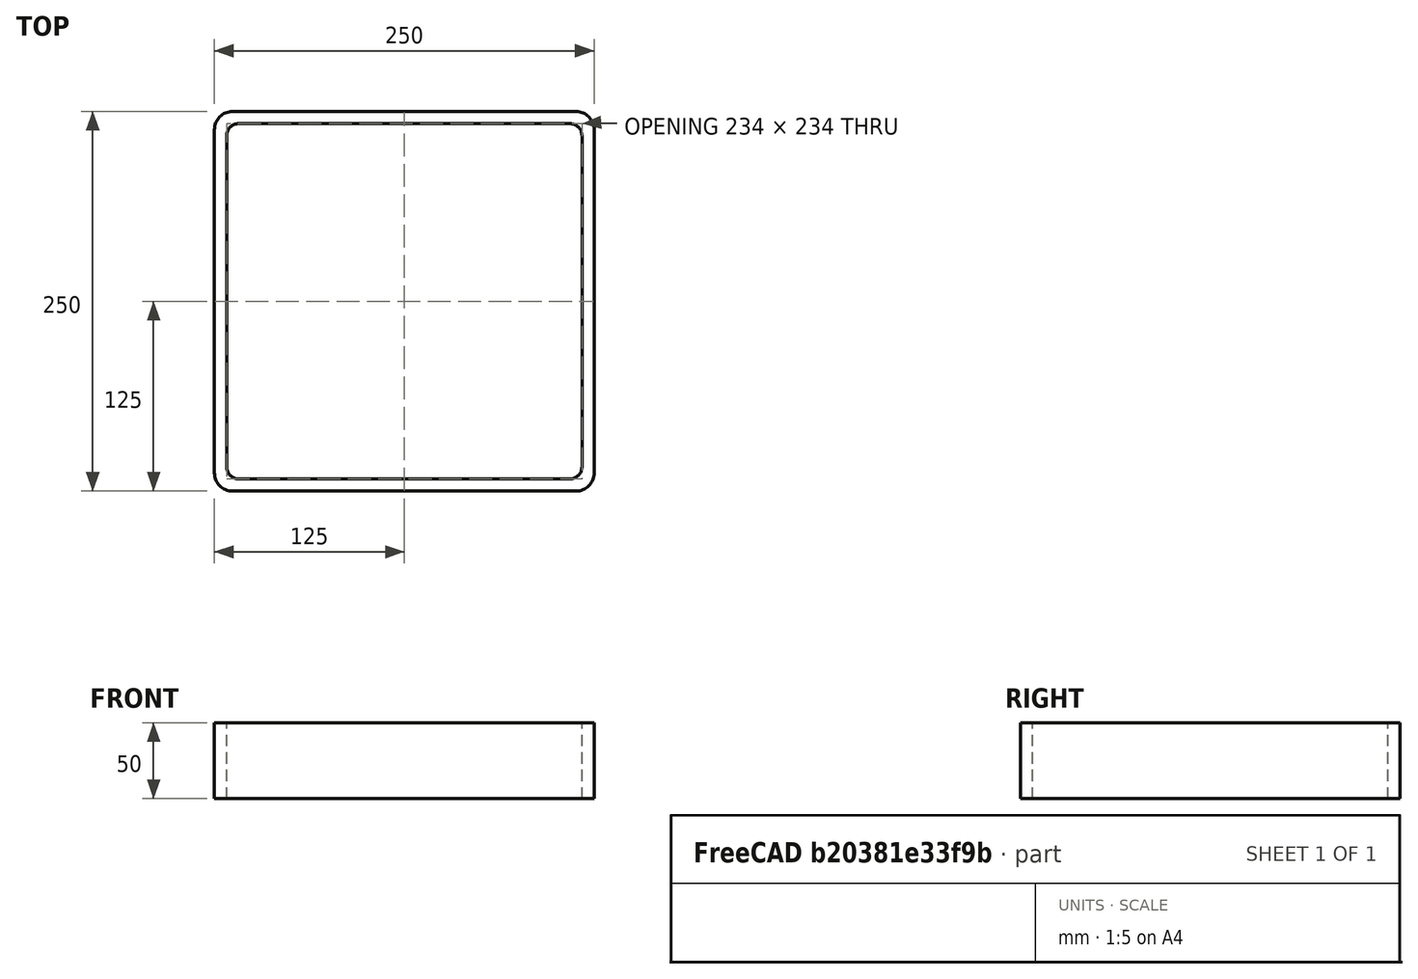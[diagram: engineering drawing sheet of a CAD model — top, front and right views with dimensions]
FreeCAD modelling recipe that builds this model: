
FCSTD DOCUMENT  (FreeCAD 0.15R4671 (Git))
Label: Square hollow section 250x250x8 EN10219 S235JRH
License: All rights reserved
LicenseURL: http://en.wikipedia.org/wiki/All_rights_reserved
objects: Sketcher::SketchObject×1, Part::Extrusion×1
note: 2 computed .brp shape members not serialized (recipe doc carries the construction recipe); baked Part::Feature solids carry a one-line shape summary decoded from their .brp

FEATURE [Sketcher::SketchObject] Sketch
  sketch-geometry (16):
    g0: LineSegment StartX=-109 StartY=117 StartZ=0 EndX=109 EndY=117 EndZ=0
    g1: LineSegment StartX=117 StartY=109 StartZ=0 EndX=117 EndY=-109 EndZ=0
    g2: LineSegment StartX=109 StartY=-117 StartZ=0 EndX=-109 EndY=-117 EndZ=0
    g3: LineSegment StartX=-117 StartY=-109 StartZ=0 EndX=-117 EndY=109 EndZ=0
    g4: LineSegment StartX=-113 StartY=125 StartZ=0 EndX=113 EndY=125 EndZ=0
    g5: LineSegment StartX=125 StartY=113 StartZ=0 EndX=125 EndY=-113 EndZ=0
    g6: LineSegment StartX=113 StartY=-125 StartZ=0 EndX=-113 EndY=-125 EndZ=0
    g7: LineSegment StartX=-125 StartY=-113 StartZ=0 EndX=-125 EndY=113 EndZ=0
    g8: ArcOfCircle CenterX=-109 CenterY=109 CenterZ=0 NormalX=0 NormalY=0 NormalZ=1 Radius=8 StartAngle=1.5708 EndAngle=3.14159
    g9: ArcOfCircle CenterX=109 CenterY=109 CenterZ=0 NormalX=0 NormalY=0 NormalZ=1 Radius=8 StartAngle=0 EndAngle=1.5708
    g10: ArcOfCircle CenterX=109 CenterY=-109 CenterZ=0 NormalX=0 NormalY=0 NormalZ=1 Radius=8 StartAngle=4.71239 EndAngle=6.28319
    g11: ArcOfCircle CenterX=-109 CenterY=-109 CenterZ=0 NormalX=0 NormalY=0 NormalZ=1 Radius=8 StartAngle=3.14159 EndAngle=4.71239
    g12: ArcOfCircle CenterX=113 CenterY=113 CenterZ=0 NormalX=0 NormalY=0 NormalZ=1 Radius=12 StartAngle=0 EndAngle=1.5708
    g13: ArcOfCircle CenterX=113 CenterY=-113 CenterZ=0 NormalX=0 NormalY=0 NormalZ=1 Radius=12 StartAngle=4.71239 EndAngle=6.28319
    g14: ArcOfCircle CenterX=-113 CenterY=-113 CenterZ=0 NormalX=0 NormalY=0 NormalZ=1 Radius=12 StartAngle=3.14159 EndAngle=4.71239
    g15: ArcOfCircle CenterX=-113 CenterY=113 CenterZ=0 NormalX=0 NormalY=0 NormalZ=1 Radius=12 StartAngle=1.5708 EndAngle=3.14159
  constraints (36):
    c: Horizontal(g2)
    c: Vertical(g3)
    c: Horizontal(g6)
    c: Vertical(g7)
    c: Tangent(g3,g8) = 1.5708
    c: Tangent(g0,g8) = 1.5708
    c: Tangent(g0,g9) = 1.5708
    c: Tangent(g1,g9) = 1.5708
    c: Tangent(g1,g10) = 1.5708
    c: Tangent(g2,g10) = 1.5708
    c: Tangent(g2,g11) = 1.5708
    c: Tangent(g3,g11) = 1.5708
    c: Tangent(g4,g12) = 1.5708
    c: Tangent(g5,g12) = 1.5708
    c: Tangent(g5,g13) = 1.5708
    c: Tangent(g6,g13) = 1.5708
    c: Tangent(g6,g14) = 1.5708
    c: Tangent(g7,g14) = 1.5708
    c: Tangent(g7,g15) = 1.5708
    c: Tangent(g4,g15) = 1.5708
    c: Equal(g9,g8)
    c: Equal(g9,g11)
    c: Equal(g9,g10)
    c: Equal(g12,g15)
    c: Equal(g12,g14)
    c: Equal(g12,g13)
    c: Symmetric(g4,g6,g-1)
    c: Symmetric(g7,g5,g-2)
    c: DistanceY(g4,g6) = -250
    c: DistanceX(g7,g5) = 250
    c: Symmetric(g3,g1,g-2)
    c: Symmetric(g0,g2,g-1)
    c: DistanceY(g0,g4) = 8
    c: DistanceX(g5,g1) = -8
    c: Radius(g9) = 8
    c: Radius(g12) = 12
FEATURE [Part::Extrusion] Extrude  label="Square hollow section 250x250x8 EN10219 S235JRH"
  Base = -> Sketch
  Dir = (0,0,50)
  Solid = true
